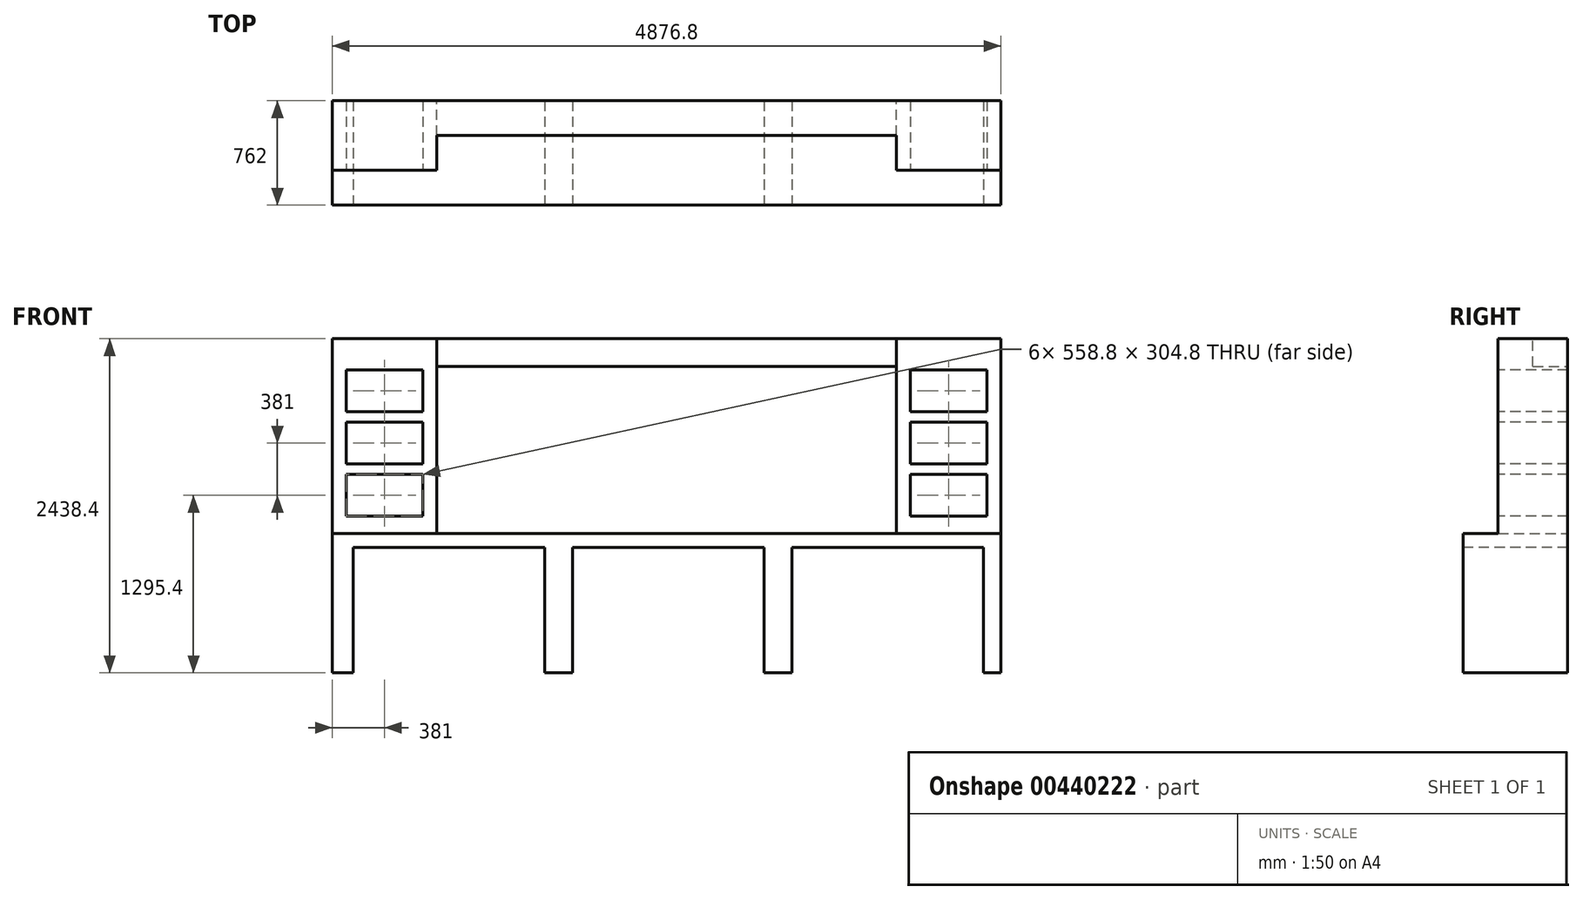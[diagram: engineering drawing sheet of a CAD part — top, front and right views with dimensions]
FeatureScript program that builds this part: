
annotation { "Feature Type Name" : "Feature", "Feature Type Description" : "" }
export const myFeature = defineFeature(function(context is Context, id is Id, definition is map)
    precondition{}
    {
        {
            var Q0;
            Q0=qCreatedBy(makeId("Front.planeOp"),FACE);
            var sketch = newSketch(context, id + "F0", { "sketchPlane" : qUnion([Q0])});
            skLineSegment(sketch, "E0.bottom", {"start": v(0, 0) * mm, "end": v(4876.8, 0) * mm});
            skLineSegment(sketch, "E0.top", {"start": v(0, 1016) * mm, "end": v(4876.8, 1016) * mm});
            skLineSegment(sketch, "E0.left", {"start": v(0, 0) * mm, "end": v(0, 1016) * mm});
            skLineSegment(sketch, "E0.right", {"start": v(4876.8, 0) * mm, "end": v(4876.8, 1016) * mm});
            skSolve(sketch);
        }
        {
            var Q0;
            Q0=makeQuery(id+"F0.imprint","IMPRINT",FACE,{"disambiguationData":[TD([[makeQuery(id+"F0.imprint","IMPRINT",EDGE,{"derivedFrom":sQuery(id+"F0.wireOp",EDGE,"E0.bottom")}),1.0]])]});
            extrude(context, id + "F1", {"entities" : qUnion([Q0]), "depth" : 762 * mm});
        }
        {
            var Q0;
            Q0=makeQuery(id+"F1.opExtrude","CAP_FACE",FACE,{"disambiguationData":[OSD([sQuery(id+"F0.wireOp",EDGE,"E0.bottom"),sQuery(id+"F0.wireOp",EDGE,"E0.top"),sQuery(id+"F0.wireOp",EDGE,"E0.left"),sQuery(id+"F0.wireOp",EDGE,"E0.right")])],"isStart":true});
            var sketch = newSketch(context, id + "F2", { "sketchPlane" : qUnion([Q0])});
            skLineSegment(sketch, "E1.bottom", {"start": v(0, 1016) * mm, "end": v(-762, 1016) * mm});
            skLineSegment(sketch, "E1.top", {"start": v(0, 2438.4) * mm, "end": v(-762, 2438.4) * mm});
            skLineSegment(sketch, "E1.left", {"start": v(0, 1016) * mm, "end": v(0, 2438.4) * mm});
            skLineSegment(sketch, "E1.right", {"start": v(-762, 1016) * mm, "end": v(-762, 2438.4) * mm});
            skLineSegment(sketch, "E2", {"start": v(-2438.4, 3145.62) * mm, "end": v(-2438.4, -1166.65) * mm, "construction": true});
            skLineSegment(sketch, "E3.MirrorCS", {"start": v(-4876.8, 2438.4) * mm, "end": v(-4114.8, 2438.4) * mm});
            skLineSegment(sketch, "E4.MirrorCS", {"start": v(-4114.8, 1016) * mm, "end": v(-4114.8, 2438.4) * mm});
            skLineSegment(sketch, "E5.MirrorCS", {"start": v(-4876.8, 1016) * mm, "end": v(-4114.8, 1016) * mm});
            skLineSegment(sketch, "E6.MirrorCS", {"start": v(-4876.8, 1016) * mm, "end": v(-4876.8, 2438.4) * mm});
            skSolve(sketch);
        }
        {
            var Q0;
            Q0=makeQuery(id+"F2.imprint","IMPRINT",FACE,{"disambiguationData":[TD([[makeQuery(id+"F2.imprint","IMPRINT",EDGE,{"derivedFrom":sQuery(id+"F2.wireOp",EDGE,"E1.bottom")}),-1.0]])]});
            var Q1;
            Q1=makeQuery(id+"F2.imprint","IMPRINT",FACE,{"disambiguationData":[TD([[makeQuery(id+"F2.imprint","IMPRINT",EDGE,{"derivedFrom":sQuery(id+"F2.wireOp",EDGE,"E3.MirrorCS")}),-1.0]])]});
            extrude(context, id + "F3", {"entities" : qUnion([Q0, Q1]), "operationType" : NewBodyOperationType.ADD, "oppositeDirection" : true, "depth" : 508 * mm});
        }
        {
            var Q0;
            Q0=makeQuery(id+"F3.boolean.opBoolean","MERGE",FACE,{"derivedFrom":[makeQuery(id+"F1.opExtrude","CAP_FACE",FACE,{"disambiguationData":[OSD([sQuery(id+"F0.wireOp",EDGE,"E0.bottom"),sQuery(id+"F0.wireOp",EDGE,"E0.top"),sQuery(id+"F0.wireOp",EDGE,"E0.left"),sQuery(id+"F0.wireOp",EDGE,"E0.right")])],"isStart":true}),makeQuery(id+"F3.opExtrude","CAP_FACE",FACE,{"disambiguationData":[OSD([sQuery(id+"F2.wireOp",EDGE,"E1.bottom"),sQuery(id+"F2.wireOp",EDGE,"E1.top"),sQuery(id+"F2.wireOp",EDGE,"E1.left"),sQuery(id+"F2.wireOp",EDGE,"E1.right")])],"isStart":true}),makeQuery(id+"F3.opExtrude","CAP_FACE",FACE,{"disambiguationData":[OSD([sQuery(id+"F2.wireOp",EDGE,"E3.MirrorCS"),sQuery(id+"F2.wireOp",EDGE,"E4.MirrorCS"),sQuery(id+"F2.wireOp",EDGE,"E5.MirrorCS"),sQuery(id+"F2.wireOp",EDGE,"E6.MirrorCS")])],"isStart":true})]});
            var sketch = newSketch(context, id + "F4", { "sketchPlane" : qUnion([Q0])});
            skLineSegment(sketch, "E7.bottom", {"start": v(-762, 2438.4) * mm, "end": v(-4114.8, 2438.4) * mm});
            skLineSegment(sketch, "E7.top", {"start": v(-762, 2235.2) * mm, "end": v(-4114.8, 2235.2) * mm});
            skLineSegment(sketch, "E7.left", {"start": v(-762, 2438.4) * mm, "end": v(-762, 2235.2) * mm});
            skLineSegment(sketch, "E7.right", {"start": v(-4114.8, 2438.4) * mm, "end": v(-4114.8, 2235.2) * mm});
            skSolve(sketch);
        }
        {
            var Q0;
            Q0=makeQuery(id+"F4.imprint","IMPRINT",FACE,{"disambiguationData":[TD([[makeQuery(id+"F4.imprint","IMPRINT",EDGE,{"derivedFrom":sQuery(id+"F4.wireOp",EDGE,"E7.bottom")}),1.0]])]});
            extrude(context, id + "F5", {"entities" : qUnion([Q0]), "operationType" : NewBodyOperationType.ADD, "oppositeDirection" : true, "depth" : 254 * mm});
        }
        {
            var Q0;
            Q0=makeQuery(id+"F1.opExtrude","CAP_FACE",FACE,{"disambiguationData":[OSD([sQuery(id+"F0.wireOp",EDGE,"E0.bottom"),sQuery(id+"F0.wireOp",EDGE,"E0.top"),sQuery(id+"F0.wireOp",EDGE,"E0.left"),sQuery(id+"F0.wireOp",EDGE,"E0.right")])],"isStart":false});
            var sketch = newSketch(context, id + "F6", { "sketchPlane" : qUnion([Q0])});
            skLineSegment(sketch, "E8.bottom", {"start": v(152.4, 0) * mm, "end": v(1549.4, 0) * mm});
            skLineSegment(sketch, "E8.top", {"start": v(152.4, 914.4) * mm, "end": v(1549.4, 914.4) * mm});
            skLineSegment(sketch, "E8.left", {"start": v(152.4, 0) * mm, "end": v(152.4, 914.4) * mm});
            skLineSegment(sketch, "E8.right", {"start": v(1549.4, 0) * mm, "end": v(1549.4, 914.4) * mm});
            skLineSegment(sketch, "E9.1.0.0", {"start": v(1752.6, 0) * mm, "end": v(1752.6, 914.4) * mm});
            skLineSegment(sketch, "E9.1.0.1", {"start": v(1752.6, 914.4) * mm, "end": v(3149.6, 914.4) * mm});
            skLineSegment(sketch, "E9.1.0.2", {"start": v(3149.6, 0) * mm, "end": v(3149.6, 914.4) * mm});
            skLineSegment(sketch, "E9.1.0.3", {"start": v(1752.6, 0) * mm, "end": v(3149.6, 0) * mm});
            skLineSegment(sketch, "E9.2.0.0", {"start": v(3352.8, 0) * mm, "end": v(3352.8, 914.4) * mm});
            skLineSegment(sketch, "E9.2.0.1", {"start": v(3352.8, 914.4) * mm, "end": v(4749.8, 914.4) * mm});
            skLineSegment(sketch, "E9.2.0.2", {"start": v(4749.8, 0) * mm, "end": v(4749.8, 914.4) * mm});
            skLineSegment(sketch, "E9.2.0.3", {"start": v(3352.8, 0) * mm, "end": v(4749.8, 0) * mm});
            skLineSegment(sketch, "E9.direction1", {"start": v(152.4, 0) * mm, "end": v(1752.6, 0) * mm, "construction": true});
            skSolve(sketch);
        }
        {
            var Q0;
            Q0=makeQuery(id+"F6.imprint","IMPRINT",FACE,{"disambiguationData":[TD([[makeQuery(id+"F6.imprint","IMPRINT",EDGE,{"derivedFrom":sQuery(id+"F6.wireOp",EDGE,"E8.bottom")}),1.0]])]});
            var Q1;
            Q1=makeQuery(id+"F6.imprint","IMPRINT",FACE,{"disambiguationData":[TD([[makeQuery(id+"F6.imprint","IMPRINT",EDGE,{"derivedFrom":sQuery(id+"F6.wireOp",EDGE,"E9.1.0.0")}),-1.0]])]});
            var Q2;
            Q2=makeQuery(id+"F6.imprint","IMPRINT",FACE,{"disambiguationData":[TD([[makeQuery(id+"F6.imprint","IMPRINT",EDGE,{"derivedFrom":sQuery(id+"F6.wireOp",EDGE,"E9.2.0.0")}),-1.0]])]});
            extrude(context, id + "F7", {"entities" : qUnion([Q0, Q1, Q2]), "operationType" : NewBodyOperationType.REMOVE, "endBound" : BoundingType.UP_TO_NEXT, "oppositeDirection" : true, "depth" : 25.4 * mm});
        }
        {
            var Q0;
            Q0=makeQuery(id+"F3.opExtrude","CAP_FACE",FACE,{"disambiguationData":[OSD([sQuery(id+"F2.wireOp",EDGE,"E1.bottom"),sQuery(id+"F2.wireOp",EDGE,"E1.top"),sQuery(id+"F2.wireOp",EDGE,"E1.left"),sQuery(id+"F2.wireOp",EDGE,"E1.right")])],"isStart":false});
            var sketch = newSketch(context, id + "F8", { "sketchPlane" : qUnion([Q0])});
            skLineSegment(sketch, "E10.bottom", {"start": v(101.6, 1143) * mm, "end": v(660.4, 1143) * mm});
            skLineSegment(sketch, "E10.top", {"start": v(101.6, 1447.8) * mm, "end": v(660.4, 1447.8) * mm});
            skLineSegment(sketch, "E10.left", {"start": v(101.6, 1143) * mm, "end": v(101.6, 1447.8) * mm});
            skLineSegment(sketch, "E10.right", {"start": v(660.4, 1143) * mm, "end": v(660.4, 1447.8) * mm});
            skLineSegment(sketch, "E11.0.1.0", {"start": v(101.6, 1828.8) * mm, "end": v(660.4, 1828.8) * mm});
            skLineSegment(sketch, "E11.0.1.1", {"start": v(660.4, 1524) * mm, "end": v(660.4, 1828.8) * mm});
            skLineSegment(sketch, "E11.0.1.2", {"start": v(101.6, 1524) * mm, "end": v(660.4, 1524) * mm});
            skLineSegment(sketch, "E11.0.1.3", {"start": v(101.6, 1524) * mm, "end": v(101.6, 1828.8) * mm});
            skLineSegment(sketch, "E11.0.2.0", {"start": v(101.6, 2209.8) * mm, "end": v(660.4, 2209.8) * mm});
            skLineSegment(sketch, "E11.0.2.1", {"start": v(660.4, 1905) * mm, "end": v(660.4, 2209.8) * mm});
            skLineSegment(sketch, "E11.0.2.2", {"start": v(101.6, 1905) * mm, "end": v(660.4, 1905) * mm});
            skLineSegment(sketch, "E11.0.2.3", {"start": v(101.6, 1905) * mm, "end": v(101.6, 2209.8) * mm});
            skLineSegment(sketch, "E11.direction1", {"start": v(101.6, 1447.8) * mm, "end": v(-508, 1447.8) * mm, "construction": true});
            skLineSegment(sketch, "E11.direction2", {"start": v(101.6, 1447.8) * mm, "end": v(101.6, 1828.8) * mm, "construction": true});
            skLineSegment(sketch, "E12", {"start": v(2438.4, 2912.67) * mm, "end": v(2438.4, -439.57) * mm, "construction": true});
            skLineSegment(sketch, "E13.MirrorCS", {"start": v(4775.2, 1143) * mm, "end": v(4216.4, 1143) * mm});
            skLineSegment(sketch, "E14.MirrorCS", {"start": v(4775.2, 1143) * mm, "end": v(4775.2, 1447.8) * mm});
            skLineSegment(sketch, "E15.MirrorCS", {"start": v(4775.2, 1447.8) * mm, "end": v(4216.4, 1447.8) * mm});
            skLineSegment(sketch, "E16.MirrorCS", {"start": v(4216.4, 1143) * mm, "end": v(4216.4, 1447.8) * mm});
            skLineSegment(sketch, "E17.MirrorCS", {"start": v(4775.2, 1524) * mm, "end": v(4216.4, 1524) * mm});
            skLineSegment(sketch, "E18.MirrorCS", {"start": v(4216.4, 1524) * mm, "end": v(4216.4, 1828.8) * mm});
            skLineSegment(sketch, "E19.MirrorCS", {"start": v(4775.2, 1828.8) * mm, "end": v(4216.4, 1828.8) * mm});
            skLineSegment(sketch, "E20.MirrorCS", {"start": v(4775.2, 1905) * mm, "end": v(4216.4, 1905) * mm});
            skLineSegment(sketch, "E21.MirrorCS", {"start": v(4775.2, 1905) * mm, "end": v(4775.2, 2209.8) * mm});
            skLineSegment(sketch, "E22.MirrorCS", {"start": v(4775.2, 2209.8) * mm, "end": v(4216.4, 2209.8) * mm});
            skLineSegment(sketch, "E23.MirrorCS", {"start": v(4216.4, 1905) * mm, "end": v(4216.4, 2209.8) * mm});
            skLineSegment(sketch, "E24", {"start": v(4775.2, 1828.8) * mm, "end": v(4775.2, 1524) * mm});
            skSolve(sketch);
        }
        {
            var Q0;
            Q0=makeQuery(id+"F8.imprint","IMPRINT",FACE,{"disambiguationData":[TD([[makeQuery(id+"F8.imprint","IMPRINT",EDGE,{"derivedFrom":sQuery(id+"F8.wireOp",EDGE,"E10.bottom")}),1.0]])]});
            var Q1;
            Q1=makeQuery(id+"F8.imprint","IMPRINT",FACE,{"disambiguationData":[TD([[makeQuery(id+"F8.imprint","IMPRINT",EDGE,{"derivedFrom":sQuery(id+"F8.wireOp",EDGE,"E11.0.1.0")}),-1.0]])]});
            var Q2;
            Q2=makeQuery(id+"F8.imprint","IMPRINT",FACE,{"disambiguationData":[TD([[makeQuery(id+"F8.imprint","IMPRINT",EDGE,{"derivedFrom":sQuery(id+"F8.wireOp",EDGE,"E11.0.2.0")}),-1.0]])]});
            var Q3;
            Q3=makeQuery(id+"F8.imprint","IMPRINT",FACE,{"disambiguationData":[TD([[makeQuery(id+"F8.imprint","IMPRINT",EDGE,{"derivedFrom":sQuery(id+"F8.wireOp",EDGE,"E13.MirrorCS")}),-1.0]])]});
            var Q4;
            Q4=makeQuery(id+"F8.imprint","IMPRINT",FACE,{"disambiguationData":[TD([[makeQuery(id+"F8.imprint","IMPRINT",EDGE,{"derivedFrom":sQuery(id+"F8.wireOp",EDGE,"E20.MirrorCS")}),-1.0]])]});
            var Q5;
            Q5=makeQuery(id+"F8.imprint","IMPRINT",FACE,{"disambiguationData":[TD([[makeQuery(id+"F8.imprint","IMPRINT",EDGE,{"derivedFrom":sQuery(id+"F8.wireOp",EDGE,"E17.MirrorCS")}),-1.0]])]});
            extrude(context, id + "F9", {"entities" : qUnion([Q0, Q1, Q2, Q3, Q4, Q5]), "operationType" : NewBodyOperationType.REMOVE, "endBound" : BoundingType.UP_TO_NEXT, "oppositeDirection" : true, "depth" : 25.4 * mm});
        }
    });
